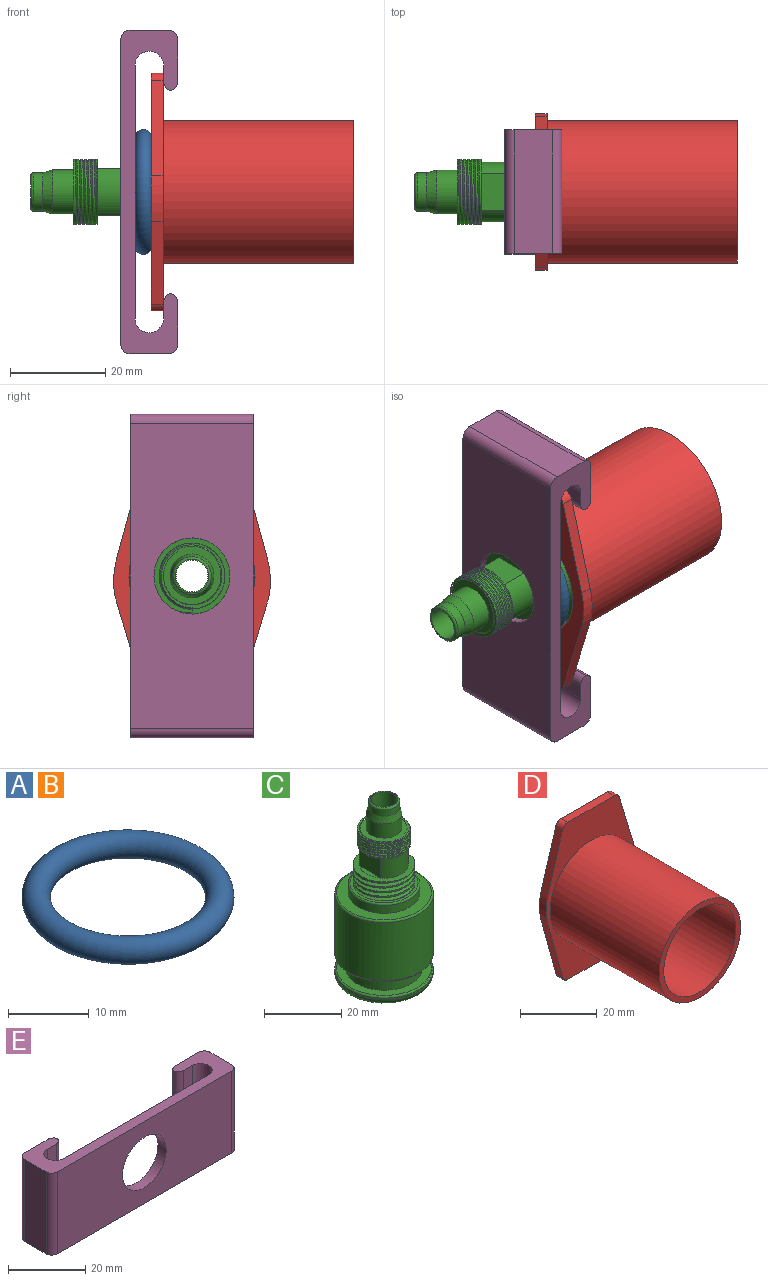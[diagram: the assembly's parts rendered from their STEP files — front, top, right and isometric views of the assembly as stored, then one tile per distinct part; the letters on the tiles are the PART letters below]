
ASSEMBLY  parts=5 mates=5
PART A: 1 faces, bbox 28.5x28.5x3.5 mm
  f0: torus R=11.4mm, axis (0,0,-1), area 787.6mm2
PART B: same geometry as A
PART C: 47 faces, bbox 51.6x51.6x80.4 mm
  f0: cylinder r=6.3mm len=10mm, axis (0,0,-1), area 75.1mm2, adj f3,f25,f38,f41
  f1: cylinder r=6.3mm len=10mm, axis (0,0,-1), area 75.1mm2, adj f3,f25,f38,f41
  f2: plane 13.8x13.8mm, normal (0,0,1), area 72mm2, adj f23,f24,f32,f33,f34,f35
  f3: plane 16.2x16.15mm, normal (0,0,1), area 75.7mm2, adj f0,f1,f4,f26,f27,f40,f42
  f4: cylinder r=8mm len=16mm, axis (0,0,-1), area 117.7mm2, adj f3,f5,f26,f27,f29,f31
  f5: plane 17.6x17.6mm, normal (0,0,1), area 42.2mm2, adj f4,f6,f28
  f6: torus R=8.8mm, axis (0,0,-1), area 45mm2, adj f5,f7
  f7: cylinder r=9.3mm len=18.6mm, axis (0,0,-1), area 146.1mm2, adj f6,f8
  f8: plane 24.5x24.5mm, normal (0,0,1), area 199.7mm2, adj f7,f9
  f9: torus R=12.25mm, axis (0,0,-1), area 62mm2, adj f8,f10
  f10: cylinder r=12.75mm len=25.5mm, axis (0,0,-1), area 1474mm2, adj f9,f45
  f11: plane 24.5x24.5mm, normal (0,0,-1), area 163.5mm2, adj f12,f45
  f12: cylinder r=9.9mm len=19.8mm, axis (0,0,-1), area 279.9mm2, adj f11,f13
  f13: plane 24.5x24.5mm, normal (0,0,1), area 163.5mm2, adj f12,f46
  f14: cylinder r=12.75mm len=25.5mm, axis (0,0,-1), area 40.1mm2, adj f15,f46
  f15: torus R=10.75mm, axis (0,0,-1), area 237.3mm2, adj f14,f16
  f16: plane 21.5x21.5mm, normal (0,0,-1), area 72.5mm2, adj f15,f17
  f17: torus R=9.62mm, axis (0,0,-1), area 37.1mm2, adj f16,f18
  f18: cone r=9.14mm half-angle=17.6deg, axis (0,0,-1), area 752.9mm2, adj f17,f19
  f19: cylinder r=3.35mm len=37.76mm, axis (0,0,-1), area 794.7mm2, adj f18,f20
  f20: plane 7.1x7.1mm, normal (0,0,1), area 4.3mm2, adj f19,f44
  f21: cylinder r=4.05mm len=8.1mm, axis (0,0,-1), area 50.9mm2, adj f22,f44
  f22: cone r=4.62mm half-angle=16deg, axis (0,0,-1), area 56.7mm2, adj f21,f23
  f23: cylinder r=4.62mm len=9.25mm, axis (0,0,-1), area 130.8mm2, adj f2,f22
  f24: cylinder r=6.9mm len=13.8mm, axis (0,0,-1), area 114.4mm2, adj f2,f25,f33,f34,f35,f36,f37
  f25: plane 37.84x37.77mm, normal (0,0,-1), area 22.9mm2, adj f0,f1,f24,f36,f37,f39,f43
  f26: plane 1x0.9mm, normal (0,-1,0), area 0.7mm2, adj f3,f4,f27,f30,f31
  f27: bspline ~18.48x16mm, area 193.8mm2, adj f3,f4,f26,f29,f30
  f28: cylinder r=8mm len=16mm, axis (0,0,-1), area 13.5mm2, adj f5,f29,f31
  f29: plane 1x1mm, normal (0,1,0), area 0.7mm2, adj f4,f27,f28,f30,f31
  f30: cylinder r=7mm len=14mm, axis (0,0,-1), area 65.4mm2, adj f26,f27,f29,f31
  f31: bspline ~18.48x16mm, area 202.1mm2, adj f4,f26,f28,f29,f30
  f32: cylinder r=6mm len=12mm, axis (0,0,-1), area 33.1mm2, adj f2,f34,f35,f37
  f33: plane 0.29x0.26mm, normal (0,-1,0), area 0mm2, adj f2,f24,f35
  f34: bspline ~16.17x14mm, area 273.4mm2, adj f2,f24,f32,f37
  f35: bspline ~16.17x14mm, area 316.5mm2, adj f2,f24,f32,f33,f37
  f36: bspline ~16.17x14mm, area 2.8mm2, adj f24,f25
  f37: plane 24.07x24.04mm, normal (1,0,0), area 0.2mm2, adj f24,f25,f32,f34,f35
  f38: plane 7.67x6.5mm, normal (1,0,0), area 49.8mm2, adj f0,f1,f39,f40
  f39: plane 7.67x1.3mm, normal (0,0,-1), area 6.8mm2, adj f25,f38
  f40: plane 7.76x1.35mm, normal (0,0,1), area 6.8mm2, adj f3,f38
  f41: plane 7.67x6.5mm, normal (-1,0,0), area 49.8mm2, adj f0,f1,f42,f43
  f42: plane 7.76x1.35mm, normal (0,0,1), area 6.8mm2, adj f3,f41
  f43: plane 7.67x1.3mm, normal (0,0,-1), area 6.8mm2, adj f25,f41
  f44: torus R=3.55mm, axis (0,0,-1), area 19.1mm2, adj f20,f21
  f45: torus R=12.25mm, axis (0,0,1), area 62mm2, adj f10,f11
  f46: torus R=12.25mm, axis (0,0,1), area 62mm2, adj f13,f14
PART D: 19 faces, bbox 33x42.5x50 mm
  f0: cylinder r=13.25mm len=26.5mm, axis (0,-1,0), area 166.5mm2, adj f10,f14
  f1: plane 20.16x5.51mm, normal (-0.96,0,-0.26), area 52.3mm2, adj f8,f9,f10,f15
  f2: plane 16.95x2.5mm, normal (0,0,-1), area 42.4mm2, adj f9,f10,f15,f16
  f3: plane 20.16x5.51mm, normal (0.96,0,-0.26), area 52.3mm2, adj f4,f9,f10,f16
  f4: cylinder r=16.5mm len=9.53mm, axis (0,1,0), area 24.2mm2, adj f3,f5,f9,f10
  f5: plane 17.41x5.24mm, normal (0.96,0,0.29), area 45.5mm2, adj f4,f9,f10,f17
  f6: plane 17.03x2.5mm, normal (0,0,1), area 42.6mm2, adj f9,f10,f17,f18
  f7: plane 17.36x5.22mm, normal (-0.96,0,0.29), area 45.3mm2, adj f8,f9,f10,f18
  f8: cylinder r=16.5mm len=9.58mm, axis (0,1,0), area 24.3mm2, adj f1,f7,f9,f10
  f9: plane 50x33mm, normal (0,-1,0), area 645.5mm2, adj f1,f2,f3,f4,f5,f6,f7,f8
  f10: plane 50x33mm, normal (0,1,0), area 800.8mm2, adj f0,f1,f2,f3,f4,f5,f6,f7
  f11: cylinder r=13.25mm len=38.5mm, axis (0,-1,0), area 3205.2mm2, adj f13,f14
  f12: cylinder r=15mm len=40mm, axis (0,1,0), area 3769.9mm2, adj f9,f13
  f13: plane 30x30mm, normal (0,-1,0), area 155.3mm2, adj f11,f12
  f14: torus R=14mm, axis (0,1,0), area 188.2mm2, adj f0,f11
  f15: cylinder r=2mm len=2.5mm, axis (0,-1,0), area 6.5mm2, adj f1,f2,f9,f10
  f16: cylinder r=2mm len=2.5mm, axis (0,1,0), area 6.5mm2, adj f2,f3,f9,f10
  f17: cylinder r=2mm len=2.5mm, axis (0,-1,0), area 6.4mm2, adj f5,f6,f9,f10
  f18: cylinder r=2mm len=2.5mm, axis (0,1,0), area 6.4mm2, adj f6,f7,f9,f10
PART E: 21 faces, bbox 68x12x26 mm
  f0: plane 26x8.73mm, normal (0,1,0), area 227.1mm2, adj f1,f2,f13,f18
  f1: plane 68x12mm, normal (0,0,-1), area 334.4mm2, adj f0,f3,f4,f6,f7,f8,f9,f10
  f2: plane 68x12mm, normal (0,0,1), area 334.4mm2, adj f0,f3,f4,f6,f7,f8,f9,f10
  f3: plane 26x8mm, normal (-1,0,0), area 208mm2, adj f1,f2,f18,f20
  f4: plane 26x8mm, normal (1,0,0), area 208mm2, adj f1,f2,f17,f19
  f5: cylinder r=8mm len=16mm, axis (0,1,0), area 150.8mm2, adj f6,f10
  f6: plane 64x26mm, normal (0,-1,0), area 1462.9mm2, adj f1,f2,f5,f19,f20
  f7: plane 26x8.73mm, normal (0,1,0), area 227.1mm2, adj f1,f2,f15,f17
  f8: plane 26x3.3mm, normal (0,-1,0), area 85.9mm2, adj f1,f2,f9,f14
  f9: cylinder r=3mm len=26mm, axis (0,0,1), area 245mm2, adj f1,f2,f8,f10
  f10: plane 53.14x26mm, normal (0,1,0), area 1180.6mm2, adj f1,f2,f5,f9,f11
  f11: cylinder r=3mm len=26mm, axis (0,0,1), area 245mm2, adj f1,f2,f10,f12
  f12: plane 26x3.3mm, normal (0,-1,0), area 85.9mm2, adj f1,f2,f11,f16
  f13: cylinder r=2mm len=26mm, axis (0,0,-1), area 68.5mm2, adj f0,f1,f2,f14
  f14: cylinder r=2mm len=26mm, axis (0,0,1), area 68.5mm2, adj f1,f2,f8,f13
  f15: cylinder r=2mm len=26mm, axis (0,0,-1), area 68.5mm2, adj f1,f2,f7,f16
  f16: cylinder r=2mm len=26mm, axis (0,0,1), area 68.5mm2, adj f1,f2,f12,f15
  f17: cylinder r=2mm len=26mm, axis (0,0,1), area 81.7mm2, adj f1,f2,f4,f7
  f18: cylinder r=2mm len=26mm, axis (0,0,-1), area 81.7mm2, adj f0,f1,f2,f3
  f19: cylinder r=2mm len=26mm, axis (0,0,-1), area 81.7mm2, adj f1,f2,f4,f6
  f20: cylinder r=2mm len=26mm, axis (0,0,1), area 81.7mm2, adj f1,f2,f3,f6
PLACE A rot(axis=(-0.58,-0.58,0.58),120deg) t=(-15.56,0,0)mm
PLACE B rot(axis=(-0.58,-0.58,0.58),120deg) t=(15.83,0,0)mm
PLACE C rot(axis=(0.71,0,-0.71),180deg) t=(4.2,0,0)mm
PLACE D rot(axis=(0.71,-0.71,0),180deg) t=(-13.86,0,0)mm
PLACE E rot(axis=(0.58,0.58,-0.58),120deg) t=(-8.25,0,0)mm
MATE slider E.f5 <-> C.f0  axis (1,0,0) through (-20.25,0,0)mm
MATE parallel D.f2 <-> E.f3  axis (0,0,1) through (-12.61,0,25)mm
MATE slider D.f0 <-> B.f0  axis (-1,0,0) through (8.64,0,0)mm
MATE cylindrical D.f0 <-> C.f0  axis (-1,0,0) through (-13.86,0,0)mm
MATE cylindrical A.f0 <-> C.f0  axis (1,0,0) through (-15.56,0,0)mm
